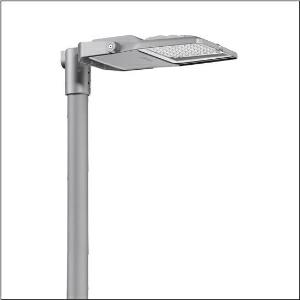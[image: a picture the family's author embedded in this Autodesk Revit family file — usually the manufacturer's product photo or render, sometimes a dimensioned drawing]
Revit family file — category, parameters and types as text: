
# Revit family: floodlight_fl_21_mini___pl64_5xa7776d2e3a_9c1a
name_source: partatom
category: Lighting Fixtures
units: mm (PartAtom-declared; Revit-internal decimal feet)

## family parameters
Cut with Voids When Loaded = No
Host = Face
Light Source = No
Part Type = Normal
Room Calculation Point = No
Round Connector Dimension = Use Diameter
Shared = No

## types (1)
- --- (1 x LED, 17220 lm, 142.9 W, 3000K)
    Apparent Load = 143 VA
    CIE Flux Codes = 28 80 98 100 100
    Color Rendering = 70
    Color Temperature = 3000K
    Default Elevation = 1800 mm
    Description = Floodlight FL 21 mini, floodlight, primary light control with lens, of PMMA, primary optical cover: protective disc, of toughened safety glass, transparent, light distribution: PL64, light emission: direct distribution, installation type: surface-mounted, LED, High Power LED, rated luminous flux: 17.220lm, luminous efficacy: 121lm/W, light colour: 730, colour temperature: 3000K, control: flexible luminous flux parameterisation, time-dependent luminous flux control, constant luminous flux control, overheat protection, pre-setting: logarithmic dimming characteristic, with terminal, 6-pole, mains connection: 220..240V, AC, 50/60Hz, start of lifetime: 143W, end of service life: 151W, reduction: 63W, luminaire housing, of diecast aluminium, powder-coated, Siteco® metallic grey (DB 702S), corrosivity category C5 mid according to DIN EN ISO 12944, sealing non-destructively replaceable, please order mast flange separately, mast bracket, of steel, galvanised, powder-coated, Siteco® metallic grey (DB 702S), Smart Interface below and above, protection rating (complete): IP66, insulation class (complete): insulation class II (safety insulation), certification: CE, ENEC, VDE, protection symbol: D, impact resistance: IK08, permissible operating ambient temperature: -40..+40°C, permissible operating ambient temperature for outdoor applications: -40..+50°C, standard: DIN EN 12944, LABS conformity tested according to VDMA 24364:2018-05, packaging unit: 1 piece

Light Distribution: PL64
    Height = 70 mm
    Lamp = 1 x LED
    Lamp Light Flux = 17220 lm
    Lamp Power = 142.9 W
    Lamp count = 1
    Length = 485 mm
    Luminous efficacy = 121 lm/W
    Manufacturer = Siteco
    ModVariant = No
    Model = 5XA7776D2E3A
    Number of Poles = 1
    OnlyDefault = Yes
    Power Factor = 1
    Product Name = Floodlight FL 21 mini | PL64
    Product group = floodlight | pylon annexe
    ProductGroupID = 6200
    Protection Class = Protection class II
    Protection Degree = IP 66
    RLX_Detail_Level = 1
    RLX_Emergency_Light_Flux = 0 lm
    RLX_Emergency_Type = 0
    RLX_Emergency_Type_DB = No
    RlxData = <blob elided: 101373 chars, md5=e48b05ed>
    Socket = socket
    Standby Power = 0 W
    System Light Flux = 17220 lm
    System Power = 143 W
    Type Comments = factory setting: luminous flux: 100 % | dim-lin: 254 | 730 mA
    Type Image = l_1007125.jpg
    URL = http://relux.com
    VarID = @adj_135537
    Voltage = 0 V
    Weight = 0.00 kg
    Width = 337 mm

## geometry (parser evidence)
native form markers: Blend x4, Sweep x11
no freeform markers — native parametric forms only
